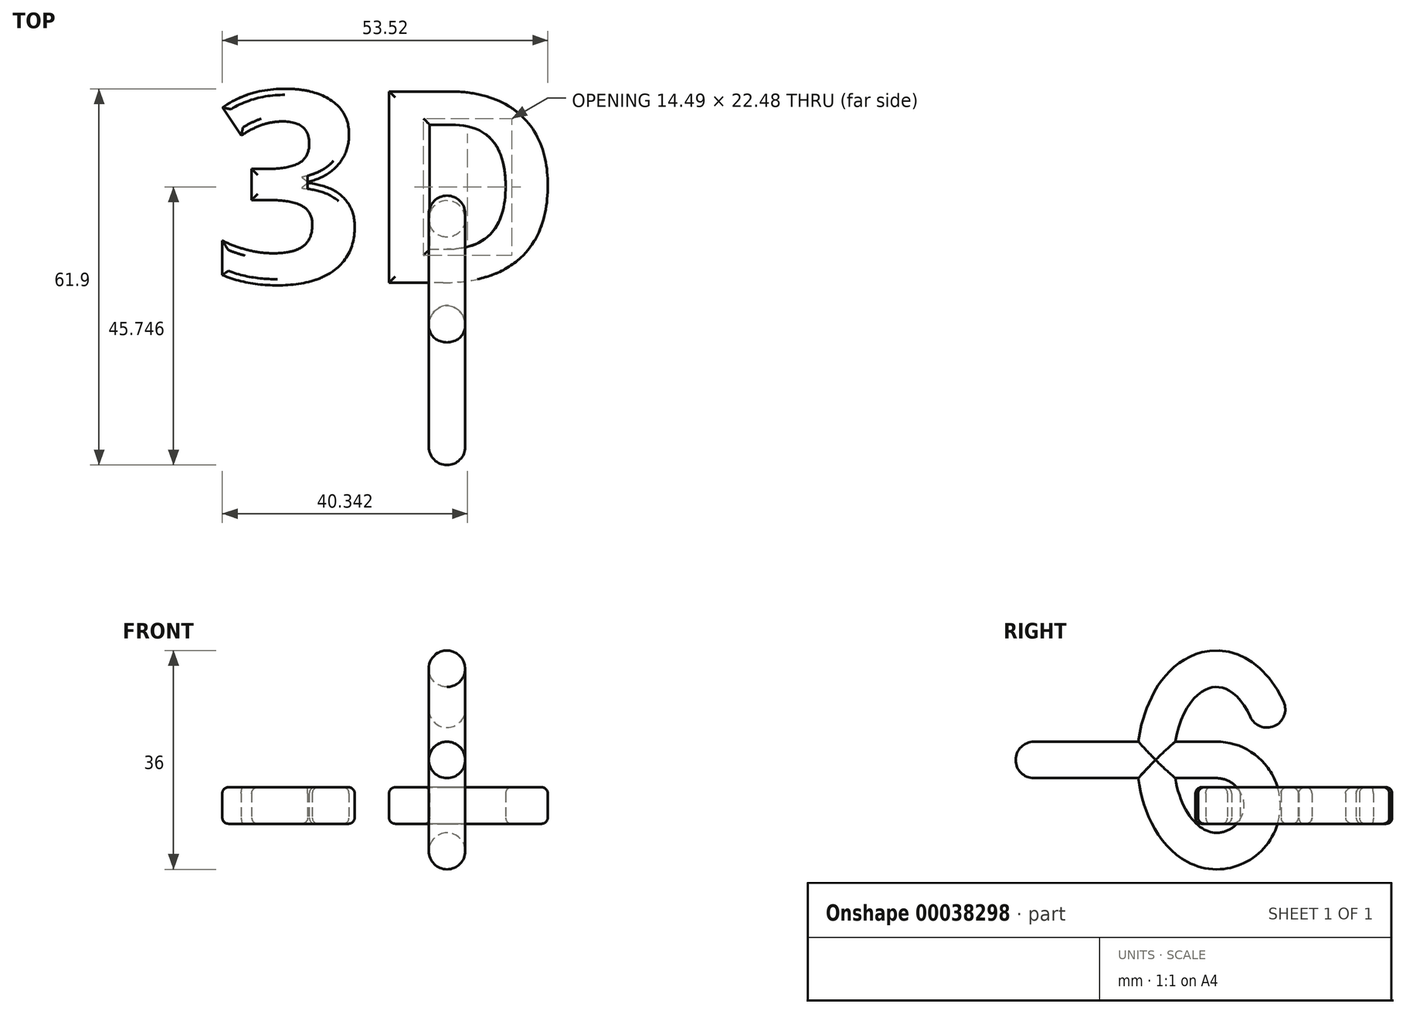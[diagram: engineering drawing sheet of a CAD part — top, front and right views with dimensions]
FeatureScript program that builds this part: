
annotation { "Feature Type Name" : "Feature", "Feature Type Description" : "" }
export const myFeature = defineFeature(function(context is Context, id is Id, definition is map)
    precondition{}
    {
        {
            var Q0;
            Q0=qCreatedBy(makeId("Top.planeOp"),FACE);
            var sketch = newSketch(context, id + "F0", { "sketchPlane" : qUnion([Q0])});
            skText(sketch, "E0", { "text": "3D", "fontName": "OpenSans-Bold.ttf"});
            const initialGuessF0  = {"E0": [-0.0552, 0, 1, 0, 0.03172]};
            skSetInitialGuess(sketch, initialGuessF0);
            skSolve(sketch);
        }
        {
            var Q0;
            Q0=makeQuery(id+"F0.imprint","IMPRINT",FACE,{"disambiguationData":[TD([[makeQuery(id+"F0.imprint","IMPRINT",EDGE,{"derivedFrom":sQuery(id+"F0.wireOp",EDGE,"E0.sketch_text.stroke-0")}),-1.0]])]});
            var Q1;
            Q1=makeQuery(id+"F0.imprint","IMPRINT",FACE,{"disambiguationData":[TD([[makeQuery(id+"F0.imprint","IMPRINT",EDGE,{"derivedFrom":sQuery(id+"F0.wireOp",EDGE,"1949aad5-839d-4fb3-a845-ca18cb88f10a.sketch_text.stroke-0")}),-1.0]])]});
            var Q2;
            Q2=makeQuery(id+"F0.imprint","IMPRINT",FACE,{"disambiguationData":[TD([[makeQuery(id+"F0.imprint","IMPRINT",EDGE,{"derivedFrom":sQuery(id+"F0.wireOp",EDGE,"1949aad5-839d-4fb3-a845-ca18cb88f10a.sketch_text.stroke-9")}),-1.0]])]});
            var Q3;
            Q3=makeQuery(id+"F0.imprint","IMPRINT",FACE,{"disambiguationData":[TD([[makeQuery(id+"F0.imprint","IMPRINT",EDGE,{"derivedFrom":sQuery(id+"F0.wireOp",EDGE,"1949aad5-839d-4fb3-a845-ca18cb88f10a.sketch_text.stroke-41")}),-1.0]])]});
            var Q4;
            Q4=makeQuery(id+"F0.imprint","IMPRINT",FACE,{"disambiguationData":[TD([[makeQuery(id+"F0.imprint","IMPRINT",EDGE,{"derivedFrom":sQuery(id+"F0.wireOp",EDGE,"E0.sketch_text.stroke-27")}),-1.0]])]});
            var Q5;
            Q5=makeQuery(id+"F0.imprint","IMPRINT",FACE,{"disambiguationData":[TD([[makeQuery(id+"F0.imprint","IMPRINT",EDGE,{"derivedFrom":sQuery(id+"F0.wireOp",EDGE,"1949aad5-839d-4fb3-a845-ca18cb88f10a.sketch_text.stroke-16")}),-1.0]])]});
            extrude(context, id + "F1", {"entities" : qUnion([Q0, Q1, Q2, Q3, Q4, Q5]), "depth" : 6 * mm});
        }
        {
            var Q0;
            Q0=makeQuery(id+"F1.opExtrude","SWEPT_EDGE",EDGE,{"disambiguationData":[OSD([sQuery(id+"F0.wireOp",EDGE,"E0.sketch_text.stroke-37"),sQuery(id+"F0.wireOp",EDGE,"E0.sketch_text.stroke-38")])]});
            cPlane(context, id + "F2", {"entities" : qUnion([Q0]), "cplaneType" : CPlaneType.LINE_ANGLE, "offset" : 150 * mm, "angle" : 0 * degree, "width" : 150 * mm, "height" : 150 * mm});
        }
        {
            var Q0;
            Q0=qCreatedBy(id+"F2.planeOp",FACE);
            var sketch = newSketch(context, id + "F3", { "sketchPlane" : qUnion([Q0])});
            skEllipticalArc(sketch, "E1", {});
            skLineSegment(sketch, "E2", {"start": v(-3, 10.5) * mm, "end": v(27, 10.5) * mm});
            skPoint(sketch, "E2.endSnap0", {"position": v(7, 10.5) * mm});
            skArc(sketch, "E3", {"start": v(-3, 10.5) * mm, "mid": v(-10.5, 3) * mm, "end": v(-3, -4.5) * mm});
            skPoint(sketch, "E4", {"position": v(-11.32, 18.82) * mm});
            skLineSegment(sketch, "E5", {"start": v(-11.32, 18.82) * mm, "end": v(-3, 10.5) * mm, "construction": true});
            skPoint(sketch, "E6", {"position": v(-4.13, 3) * mm});
            const initialGuessF3  = {"E1": [-0.003, 0.0105, 0, -1, 0.015, 0.01, 0, 4.124386376837123]};
            skSetInitialGuess(sketch, initialGuessF3);
            skSolve(sketch);
        }
        {
            var Q0;
            Q0=sQuery(id+"F3.wireOp",VERTEX,"E2.end");
            var Q1;
            Q1=qCreatedBy(makeId("Front.planeOp"),FACE);
            cPlane(context, id + "F4", {"entities" : qUnion([Q0, Q1]), "cplaneType" : CPlaneType.PLANE_POINT, "offset" : 150 * mm, "width" : 150 * mm, "height" : 150 * mm});
        }
        {
            var Q0;
            Q0=qCreatedBy(id+"F4.planeOp",FACE);
            var sketch = newSketch(context, id + "F5", { "sketchPlane" : qUnion([Q0])});
            skCircle(sketch, "E7", {"center": v(-16.57, 10.5) * mm, "radius": 3 * mm});
            skSolve(sketch);
        }
        {
            var Q0;
            Q0=makeQuery(id+"F5.imprint","IMPRINT",FACE,{"disambiguationData":[TD([[makeQuery(id+"F5.imprint","IMPRINT",EDGE,{"derivedFrom":sQuery(id+"F5.wireOp",EDGE,"E7")}),1.0]])]});
            var Q1;
            Q1=sQuery(id+"F3.wireOp",EDGE,"E2");
            var Q2;
            Q2=sQuery(id+"F3.wireOp",EDGE,"E3");
            sweep(context, id + "F6", {"profiles" : qUnion([Q0]), "path" : qUnion([Q1, Q2])});
        }
        {
            var Q0;
            Q0=makeQuery(id+"F6.opSweep","CAP_FACE",FACE,{"disambiguationData":[OSD([sQuery(id+"F3.wireOp",VERTEX,"E3.end"),sQuery(id+"F5.wireOp",EDGE,"E7")])],"isStart":false});
            var Q1;
            Q1=sQuery(id+"F3.wireOp",EDGE,"E1");
            sweep(context, id + "F7", {"operationType" : NewBodyOperationType.ADD, "profiles" : qUnion([Q0]), "path" : qUnion([Q1])});
        }
        {
            var Q0;
            Q0=makeQuery(id+"F1.opExtrude","CAP_EDGE",EDGE,{"disambiguationData":[OSD([sQuery(id+"F0.wireOp",EDGE,"E0.sketch_text.stroke-6")])],"isStart":false});
            var Q1;
            Q1=makeQuery(id+"F1.opExtrude","CAP_EDGE",EDGE,{"disambiguationData":[OSD([sQuery(id+"F0.wireOp",EDGE,"E0.sketch_text.stroke-0")])],"isStart":false});
            var Q2;
            Q2=makeQuery(id+"F1.opExtrude","CAP_EDGE",EDGE,{"disambiguationData":[OSD([sQuery(id+"F0.wireOp",EDGE,"E0.sketch_text.stroke-23")])],"isStart":false});
            var Q3;
            Q3=makeQuery(id+"F1.opExtrude","CAP_EDGE",EDGE,{"disambiguationData":[OSD([sQuery(id+"F0.wireOp",EDGE,"E0.sketch_text.stroke-21")])],"isStart":false});
            var Q4;
            Q4=makeQuery(id+"F1.opExtrude","CAP_EDGE",EDGE,{"disambiguationData":[OSD([sQuery(id+"F0.wireOp",EDGE,"E0.sketch_text.stroke-16")])],"isStart":false});
            var Q5;
            Q5=makeQuery(id+"F1.opExtrude","CAP_EDGE",EDGE,{"disambiguationData":[OSD([sQuery(id+"F0.wireOp",EDGE,"E0.sketch_text.stroke-14")])],"isStart":false});
            var Q6;
            Q6=makeQuery(id+"F1.opExtrude","CAP_EDGE",EDGE,{"disambiguationData":[OSD([sQuery(id+"F0.wireOp",EDGE,"E0.sketch_text.stroke-8")])],"isStart":false});
            var Q7;
            Q7=makeQuery(id+"F1.opExtrude","CAP_EDGE",EDGE,{"disambiguationData":[OSD([sQuery(id+"F0.wireOp",EDGE,"E0.sketch_text.stroke-30")])],"isStart":false});
            var Q8;
            Q8=makeQuery(id+"F1.opExtrude","CAP_EDGE",EDGE,{"disambiguationData":[OSD([sQuery(id+"F0.wireOp",EDGE,"E0.sketch_text.stroke-31")])],"isStart":false});
            var Q9;
            Q9=makeQuery(id+"F1.opExtrude","CAP_EDGE",EDGE,{"disambiguationData":[OSD([sQuery(id+"F0.wireOp",EDGE,"E0.sketch_text.stroke-36")])],"isStart":false});
            var Q10;
            Q10=makeQuery(id+"F1.opExtrude","CAP_EDGE",EDGE,{"disambiguationData":[OSD([sQuery(id+"F0.wireOp",EDGE,"E0.sketch_text.stroke-35")])],"isStart":false});
            var Q11;
            Q11=makeQuery(id+"F1.opExtrude","CAP_FACE",FACE,{"disambiguationData":[OSD([sQuery(id+"F0.wireOp",EDGE,"E0.sketch_text.stroke-27"),sQuery(id+"F0.wireOp",EDGE,"E0.sketch_text.stroke-28"),sQuery(id+"F0.wireOp",EDGE,"E0.sketch_text.stroke-29"),sQuery(id+"F0.wireOp",EDGE,"E0.sketch_text.stroke-30"),sQuery(id+"F0.wireOp",EDGE,"E0.sketch_text.stroke-31"),sQuery(id+"F0.wireOp",EDGE,"E0.sketch_text.stroke-32"),sQuery(id+"F0.wireOp",EDGE,"E0.sketch_text.stroke-33"),sQuery(id+"F0.wireOp",EDGE,"E0.sketch_text.stroke-34"),sQuery(id+"F0.wireOp",EDGE,"E0.sketch_text.stroke-35"),sQuery(id+"F0.wireOp",EDGE,"E0.sketch_text.stroke-36"),sQuery(id+"F0.wireOp",EDGE,"E0.sketch_text.stroke-37"),sQuery(id+"F0.wireOp",EDGE,"E0.sketch_text.stroke-38")])],"isStart":true});
            var Q12;
            Q12=makeQuery(id+"F1.opExtrude","CAP_FACE",FACE,{"disambiguationData":[OSD([sQuery(id+"F0.wireOp",EDGE,"E0.sketch_text.stroke-0"),sQuery(id+"F0.wireOp",EDGE,"E0.sketch_text.stroke-1"),sQuery(id+"F0.wireOp",EDGE,"E0.sketch_text.stroke-2"),sQuery(id+"F0.wireOp",EDGE,"E0.sketch_text.stroke-3"),sQuery(id+"F0.wireOp",EDGE,"E0.sketch_text.stroke-4"),sQuery(id+"F0.wireOp",EDGE,"E0.sketch_text.stroke-5"),sQuery(id+"F0.wireOp",EDGE,"E0.sketch_text.stroke-6"),sQuery(id+"F0.wireOp",EDGE,"E0.sketch_text.stroke-7"),sQuery(id+"F0.wireOp",EDGE,"E0.sketch_text.stroke-8"),sQuery(id+"F0.wireOp",EDGE,"E0.sketch_text.stroke-9"),sQuery(id+"F0.wireOp",EDGE,"E0.sketch_text.stroke-10"),sQuery(id+"F0.wireOp",EDGE,"E0.sketch_text.stroke-11"),sQuery(id+"F0.wireOp",EDGE,"E0.sketch_text.stroke-12"),sQuery(id+"F0.wireOp",EDGE,"E0.sketch_text.stroke-13"),sQuery(id+"F0.wireOp",EDGE,"E0.sketch_text.stroke-14"),sQuery(id+"F0.wireOp",EDGE,"E0.sketch_text.stroke-15"),sQuery(id+"F0.wireOp",EDGE,"E0.sketch_text.stroke-16"),sQuery(id+"F0.wireOp",EDGE,"E0.sketch_text.stroke-17"),sQuery(id+"F0.wireOp",EDGE,"E0.sketch_text.stroke-18"),sQuery(id+"F0.wireOp",EDGE,"E0.sketch_text.stroke-19"),sQuery(id+"F0.wireOp",EDGE,"E0.sketch_text.stroke-20"),sQuery(id+"F0.wireOp",EDGE,"E0.sketch_text.stroke-21"),sQuery(id+"F0.wireOp",EDGE,"E0.sketch_text.stroke-22"),sQuery(id+"F0.wireOp",EDGE,"E0.sketch_text.stroke-23"),sQuery(id+"F0.wireOp",EDGE,"E0.sketch_text.stroke-24"),sQuery(id+"F0.wireOp",EDGE,"E0.sketch_text.stroke-25"),sQuery(id+"F0.wireOp",EDGE,"E0.sketch_text.stroke-26")])],"isStart":true});
            fillet(context, id + "F8", {"entities" : qUnion([Q0, Q1, Q2, Q3, Q4, Q5, Q6, Q7, Q8, Q9, Q10, Q11, Q12]), "radius" : 1 * mm, "tangentPropagation" : true, "allowEdgeOverflow" : false});
        }
        {
            var Q0;
            Q0=makeQuery(id+"F6.opSweep","CAP_FACE",FACE,{"disambiguationData":[OSD([sQuery(id+"F3.wireOp",VERTEX,"E2.end"),sQuery(id+"F5.wireOp",EDGE,"E7")])],"isStart":true});
            var sketch = newSketch(context, id + "F9", { "sketchPlane" : qUnion([Q0])});
            skLineSegment(sketch, "E8", {"start": v(-16.57, 13.5) * mm, "end": v(-16.57, 7.5) * mm});
            skSolve(sketch);
        }
        {
            var Q0;
            {var subQ1=sQuery(id+"F9.wireOp",EDGE,"E8");Q0=makeQuery(id+"F9.imprint","IMPRINT",FACE,{"disambiguationData":[TD([[makeQuery(id+"F9.imprint","IMPRINT",EDGE,{"derivedFrom":subQ1}),-1.0]])]});}
            var Q1;
            Q1=sQuery(id+"F9.wireOp",EDGE,"E8");
            revolve(context, id + "F10", {"operationType" : NewBodyOperationType.ADD, "entities" : qUnion([Q0]), "axis" : qUnion([Q1]), "revolveType" : RevolveType.FULL});
        }
        {
            var Q0;
            Q0=makeQuery(id+"F7.opSweep","CAP_FACE",FACE,{"disambiguationData":[OSD([sQuery(id+"F3.wireOp",VERTEX,"E1.end"),sQuery(id+"F3.wireOp",VERTEX,"E3.end"),sQuery(id+"F5.wireOp",EDGE,"E7")])],"isStart":false});
            var sketch = newSketch(context, id + "F11", { "sketchPlane" : qUnion([Q0])});
            skLineSegment(sketch, "E9", {"start": v(-13.57, -17.99) * mm, "end": v(-19.57, -17.99) * mm});
            skSolve(sketch);
        }
        {
            var Q0;
            {var subQ1=sQuery(id+"F11.wireOp",EDGE,"E9");Q0=makeQuery(id+"F11.imprint","IMPRINT",FACE,{"disambiguationData":[TD([[makeQuery(id+"F11.imprint","IMPRINT",EDGE,{"derivedFrom":subQ1}),-1.0]])]});}
            var Q1;
            Q1=sQuery(id+"F11.wireOp",EDGE,"E9");
            revolve(context, id + "F12", {"operationType" : NewBodyOperationType.ADD, "entities" : qUnion([Q0]), "axis" : qUnion([Q1]), "revolveType" : RevolveType.FULL});
        }
    });
